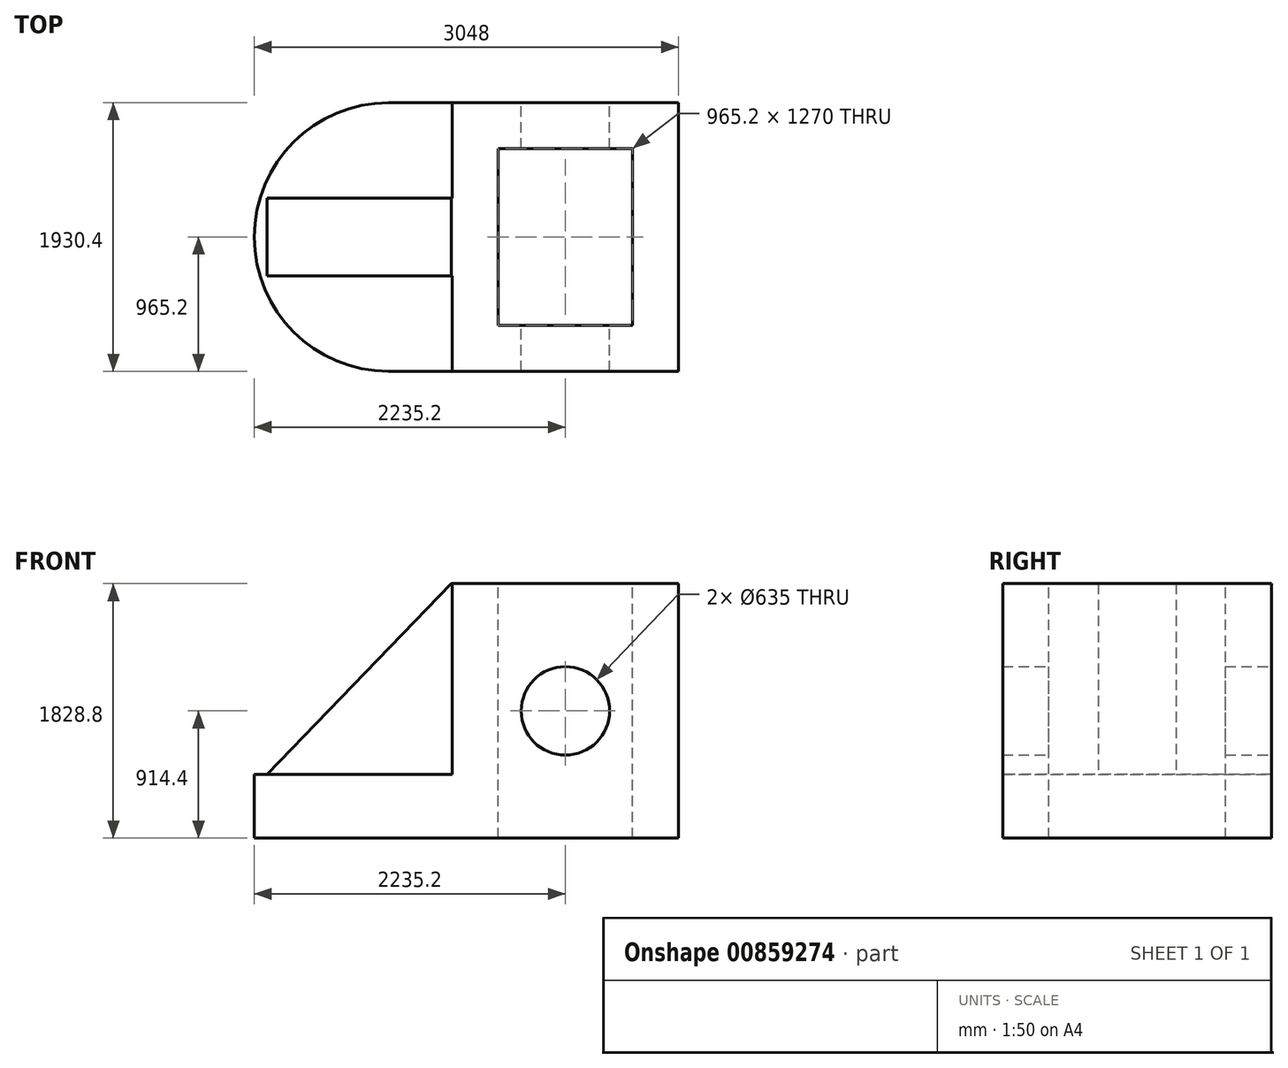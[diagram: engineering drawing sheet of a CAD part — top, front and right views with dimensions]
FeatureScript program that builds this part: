
annotation { "Feature Type Name" : "Feature", "Feature Type Description" : "" }
export const myFeature = defineFeature(function(context is Context, id is Id, definition is map)
    precondition{}
    {
        {
            var Q0;
            Q0=qCreatedBy(makeId("Front.planeOp"),FACE);
            var sketch = newSketch(context, id + "F0", { "sketchPlane" : qUnion([Q0])});
            skLineSegment(sketch, "E0.bottom", {"start": v(0, 0) * mm, "end": v(1422.4, 0) * mm});
            skLineSegment(sketch, "E0.top", {"start": v(0, 457.2) * mm, "end": v(1422.4, 457.2) * mm});
            skLineSegment(sketch, "E0.left", {"start": v(0, 0) * mm, "end": v(0, 457.2) * mm});
            skLineSegment(sketch, "E0.right", {"start": v(1422.4, 0) * mm, "end": v(1422.4, 457.2) * mm});
            skLineSegment(sketch, "E1.bottom", {"start": v(1422.4, 0) * mm, "end": v(3048, 0) * mm});
            skLineSegment(sketch, "E1.top", {"start": v(1422.4, 1828.8) * mm, "end": v(3048, 1828.8) * mm});
            skLineSegment(sketch, "E1.left", {"start": v(1422.4, 0) * mm, "end": v(1422.4, 1828.8) * mm});
            skLineSegment(sketch, "E1.right", {"start": v(3048, 0) * mm, "end": v(3048, 1828.8) * mm});
            skPoint(sketch, "E2.endSnap0", {"position": v(1422.4, 914.4) * mm});
            skCircle(sketch, "E3", {"center": v(2235.2, 914.4) * mm, "radius": 317.5 * mm});
            skSolve(sketch);
        }
        {
            var Q0;
            Q0 = qSketchRegion(id + "F0", true);
            extrude(context, id + "F1", {"entities" : qUnion([Q0]), "depth" : 1930.4 * mm, "offsetDistance" : 25.4 * mm});
        }
        {
            var Q0;
            Q0=makeQuery(id+"F1.opExtrude","CAP_EDGE",EDGE,{"disambiguationData":[OSD([sQuery(id+"F0.wireOp",EDGE,"E0.left")])],"isStart":true});
            var Q1;
            Q1=makeQuery(id+"F1.opExtrude","CAP_EDGE",EDGE,{"disambiguationData":[OSD([sQuery(id+"F0.wireOp",EDGE,"E0.left")])],"isStart":false});
            fillet(context, id + "F2", {"entities" : qUnion([Q0, Q1]), "radius" : 965.2 * mm, "tangentPropagation" : true, "allowEdgeOverflow" : false});
        }
        {
            var Q0;
            Q0=makeQuery(id+"F1.opExtrude","SWEPT_FACE",FACE,{"disambiguationData":[OSD([sQuery(id+"F0.wireOp",EDGE,"E1.left")])]});
            var sketch = newSketch(context, id + "F3", { "sketchPlane" : qUnion([Q0])});
            skLineSegment(sketch, "E4", {"start": v(1930.4, 1354.59) * mm, "end": v(1244.6, 1354.59) * mm});
            skLineSegment(sketch, "E5.bottom", {"start": v(1244.6, 1828.8) * mm, "end": v(685.8, 1828.8) * mm});
            skLineSegment(sketch, "E5.top", {"start": v(1244.6, 457.2) * mm, "end": v(685.8, 457.2) * mm});
            skLineSegment(sketch, "E5.left", {"start": v(1244.6, 1828.8) * mm, "end": v(1244.6, 457.2) * mm});
            skLineSegment(sketch, "E5.right", {"start": v(685.8, 1828.8) * mm, "end": v(685.8, 457.2) * mm});
            skSolve(sketch);
        }
        {
            var Q0;
            Q0 = qSketchRegion(id + "F3", true);
            extrude(context, id + "F4", {"entities" : qUnion([Q0]), "operationType" : NewBodyOperationType.ADD, "depth" : 1330.96 * mm, "offsetDistance" : 25.4 * mm});
        }
        {
            var Q0;
            Q0=makeQuery(id+"F4.opExtrude","CAP_EDGE",EDGE,{"disambiguationData":[OSD([sQuery(id+"F3.wireOp",EDGE,"E5.bottom")])],"isStart":false});
            chamfer(context, id + "F5", {"entities" : qUnion([Q0]), "chamferType" : ChamferType.OFFSET_ANGLE, "width" : 1371.6 * mm, "oppositeDirection" : false, "angle" : 44 * degree, "tangentPropagation" : true});
        }
        {
            var Q0;
            Q0=makeQuery(id+"F4.boolean.opBoolean","MERGE",FACE,{"derivedFrom":[makeQuery(id+"F1.opExtrude","SWEPT_FACE",FACE,{"disambiguationData":[OSD([sQuery(id+"F0.wireOp",EDGE,"E1.top")])]}),makeQuery(id+"F4.opExtrude","SWEPT_FACE",FACE,{"disambiguationData":[OSD([sQuery(id+"F3.wireOp",EDGE,"E5.bottom")])]})]});
            var sketch = newSketch(context, id + "F6", { "sketchPlane" : qUnion([Q0])});
            skLineSegment(sketch, "E6.bottom", {"start": v(1752.6, -330.2) * mm, "end": v(2717.8, -330.2) * mm});
            skLineSegment(sketch, "E6.top", {"start": v(1752.6, -1600.2) * mm, "end": v(2717.8, -1600.2) * mm});
            skLineSegment(sketch, "E6.left", {"start": v(1752.6, -330.2) * mm, "end": v(1752.6, -1600.2) * mm});
            skLineSegment(sketch, "E6.right", {"start": v(2717.8, -330.2) * mm, "end": v(2717.8, -1600.2) * mm});
            skSolve(sketch);
        }
        {
            var Q0;
            Q0 = qSketchRegion(id + "F6", true);
            extrude(context, id + "F7", {"entities" : qUnion([Q0]), "operationType" : NewBodyOperationType.REMOVE, "oppositeDirection" : true, "depth" : 4841.24 * mm, "offsetDistance" : 25.4 * mm});
        }
    });
